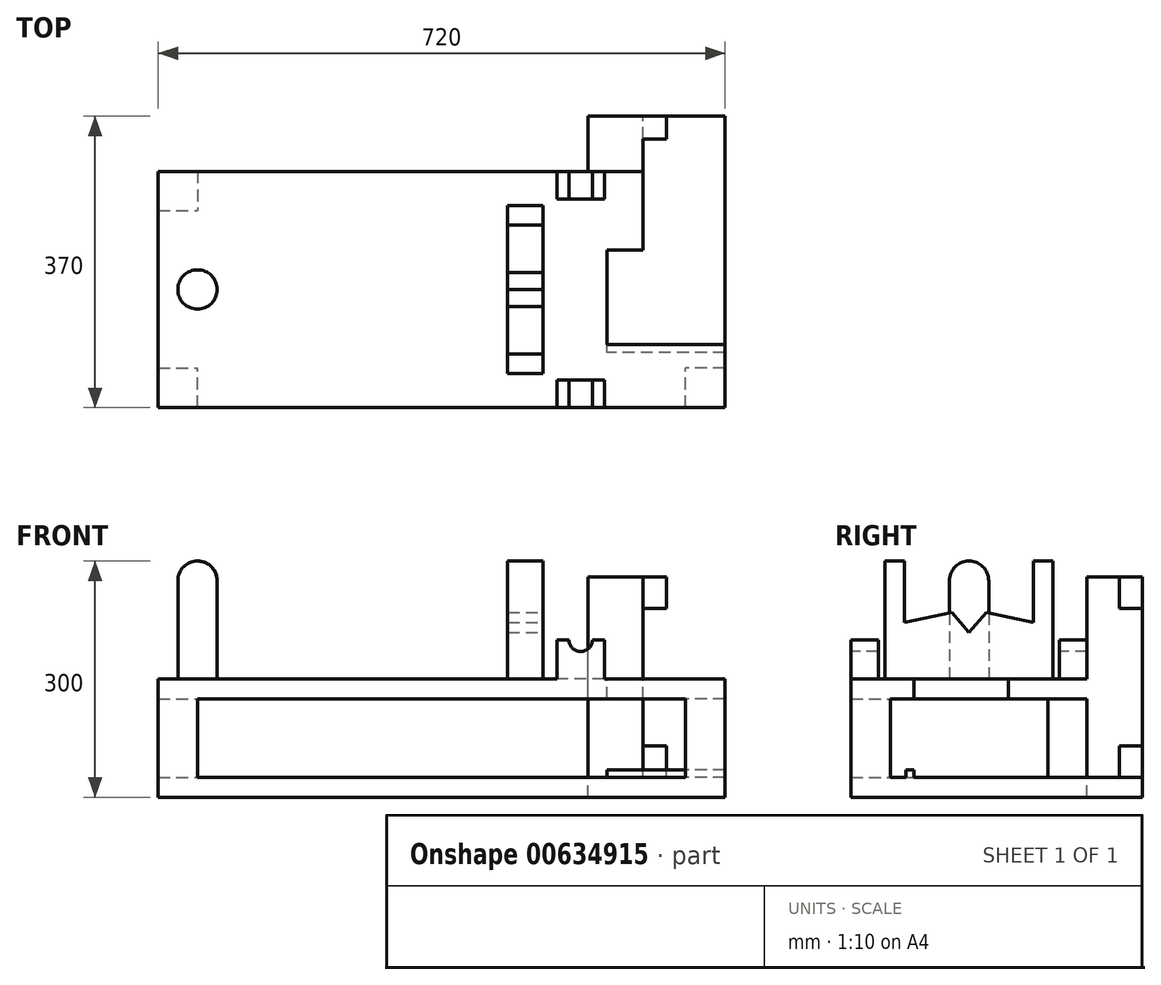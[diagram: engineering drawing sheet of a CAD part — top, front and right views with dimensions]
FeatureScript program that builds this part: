
annotation { "Feature Type Name" : "Feature", "Feature Type Description" : "" }
export const myFeature = defineFeature(function(context is Context, id is Id, definition is map)
    precondition{}
    {
        {
            var Q0;
            Q0=qCreatedBy(makeId("Top.planeOp"),FACE);
            var sketch = newSketch(context, id + "F0", { "sketchPlane" : qUnion([Q0])});
            skLineSegment(sketch, "E0.bottom", {"start": v(-360, 150) * mm, "end": v(360, 150) * mm});
            skLineSegment(sketch, "E0.top", {"start": v(-360, -150) * mm, "end": v(360, -150) * mm});
            skLineSegment(sketch, "E0.left", {"start": v(-360, 150) * mm, "end": v(-360, -150) * mm});
            skLineSegment(sketch, "E0.right", {"start": v(360, 150) * mm, "end": v(360, -150) * mm});
            skSolve(sketch);
        }
        {
            var Q0;
            Q0=makeQuery(id+"F0.imprint","IMPRINT",FACE,{"disambiguationData":[TD([[makeQuery(id+"F0.imprint","IMPRINT",EDGE,{"derivedFrom":sQuery(id+"F0.wireOp",EDGE,"E0.bottom")}),-1.0]])]});
            extrude(context, id + "F1", {"entities" : qUnion([Q0]), "depth" : 25 * mm, "offsetDistance" : 25 * mm});
        }
        {
            var Q0;
            Q0=makeQuery(id+"F1.opExtrude","CAP_FACE",FACE,{"disambiguationData":[OSD([sQuery(id+"F0.wireOp",EDGE,"E0.bottom"),sQuery(id+"F0.wireOp",EDGE,"E0.top"),sQuery(id+"F0.wireOp",EDGE,"E0.left"),sQuery(id+"F0.wireOp",EDGE,"E0.right")])],"isStart":false});
            var sketch = newSketch(context, id + "F2", { "sketchPlane" : qUnion([Q0])});
            skLineSegment(sketch, "E1.bottom", {"start": v(-360, -150) * mm, "end": v(-310, -150) * mm});
            skLineSegment(sketch, "E1.top", {"start": v(-360, -100) * mm, "end": v(-310, -100) * mm});
            skLineSegment(sketch, "E1.left", {"start": v(-360, -150) * mm, "end": v(-360, -100) * mm});
            skLineSegment(sketch, "E1.right", {"start": v(-310, -150) * mm, "end": v(-310, -100) * mm});
            skSolve(sketch);
        }
        {
            var Q0;
            Q0=makeQuery(id+"F2.imprint","IMPRINT",FACE,{"disambiguationData":[TD([[makeQuery(id+"F2.imprint","IMPRINT",EDGE,{"derivedFrom":sQuery(id+"F2.wireOp",EDGE,"E1.bottom")}),1.0]])]});
            extrude(context, id + "F3", {"entities" : qUnion([Q0]), "operationType" : NewBodyOperationType.ADD, "depth" : 100 * mm, "offsetDistance" : 25 * mm});
        }
        {
            var Q0;
            Q0=makeQuery(id+"F1.opExtrude","CAP_FACE",FACE,{"disambiguationData":[OSD([sQuery(id+"F0.wireOp",EDGE,"E0.bottom"),sQuery(id+"F0.wireOp",EDGE,"E0.top"),sQuery(id+"F0.wireOp",EDGE,"E0.left"),sQuery(id+"F0.wireOp",EDGE,"E0.right")])],"isStart":false});
            var sketch = newSketch(context, id + "F4", { "sketchPlane" : qUnion([Q0])});
            skLineSegment(sketch, "E2.bottom", {"start": v(360, -150) * mm, "end": v(310, -150) * mm});
            skLineSegment(sketch, "E2.top", {"start": v(360, -100) * mm, "end": v(310, -100) * mm});
            skLineSegment(sketch, "E2.left", {"start": v(360, -150) * mm, "end": v(360, -100) * mm});
            skLineSegment(sketch, "E2.right", {"start": v(310, -150) * mm, "end": v(310, -100) * mm});
            skLineSegment(sketch, "E3.bottom", {"start": v(360, 150) * mm, "end": v(310, 150) * mm});
            skLineSegment(sketch, "E3.top", {"start": v(360, 100) * mm, "end": v(310, 100) * mm});
            skLineSegment(sketch, "E3.left", {"start": v(360, 150) * mm, "end": v(360, 100) * mm});
            skLineSegment(sketch, "E3.right", {"start": v(310, 150) * mm, "end": v(310, 100) * mm});
            skLineSegment(sketch, "E4.bottom", {"start": v(-360, 150) * mm, "end": v(-310, 150) * mm});
            skLineSegment(sketch, "E4.top", {"start": v(-360, 100) * mm, "end": v(-310, 100) * mm});
            skLineSegment(sketch, "E4.left", {"start": v(-360, 150) * mm, "end": v(-360, 100) * mm});
            skLineSegment(sketch, "E4.right", {"start": v(-310, 150) * mm, "end": v(-310, 100) * mm});
            skSolve(sketch);
        }
        {
            var Q0;
            Q0=makeQuery(id+"F4.imprint","IMPRINT",FACE,{"disambiguationData":[TD([[makeQuery(id+"F4.imprint","IMPRINT",EDGE,{"derivedFrom":sQuery(id+"F4.wireOp",EDGE,"E2.bottom")}),1.0]])]});
            var Q1;
            Q1=makeQuery(id+"F4.imprint","IMPRINT",FACE,{"disambiguationData":[TD([[makeQuery(id+"F4.imprint","IMPRINT",EDGE,{"derivedFrom":sQuery(id+"F4.wireOp",EDGE,"E4.bottom")}),-1.0]])]});
            var Q2;
            Q2=makeQuery(id+"F4.imprint","IMPRINT",FACE,{"disambiguationData":[TD([[makeQuery(id+"F4.imprint","IMPRINT",EDGE,{"derivedFrom":sQuery(id+"F4.wireOp",EDGE,"E3.bottom")}),-1.0]])]});
            extrude(context, id + "F5", {"entities" : qUnion([Q0, Q1, Q2]), "operationType" : NewBodyOperationType.ADD, "depth" : 100 * mm, "offsetDistance" : 25 * mm});
        }
        {
            var Q0;
            Q0=makeQuery(id+"F5.opExtrude","CAP_FACE",FACE,{"disambiguationData":[OSD([sQuery(id+"F4.wireOp",EDGE,"E4.bottom"),sQuery(id+"F4.wireOp",EDGE,"E4.top"),sQuery(id+"F4.wireOp",EDGE,"E4.left"),sQuery(id+"F4.wireOp",EDGE,"E4.right")])],"isStart":false});
            var sketch = newSketch(context, id + "F6", { "sketchPlane" : qUnion([Q0])});
            skLineSegment(sketch, "E5.bottom", {"start": v(-360, 150) * mm, "end": v(360, 150) * mm});
            skLineSegment(sketch, "E5.top", {"start": v(-360, -150) * mm, "end": v(360, -150) * mm});
            skLineSegment(sketch, "E5.left", {"start": v(-360, 150) * mm, "end": v(-360, -150) * mm});
            skLineSegment(sketch, "E5.right", {"start": v(360, 150) * mm, "end": v(360, -150) * mm});
            skSolve(sketch);
        }
        {
            var Q0;
            {var subQ4=makeQuery(id+"F5.opExtrude","CAP_EDGE",EDGE,{"disambiguationData":[OSD([sQuery(id+"F4.wireOp",EDGE,"E4.top")])],"isStart":false});Q0=makeQuery(id+"F6.imprint","IMPRINT",FACE,{"disambiguationData":[TD([[makeQuery(id+"F6.imprint","IMPRINT",EDGE,{"derivedFrom":subQ4}),1.0]])]});}
            var Q1;
            {var subQ3=sQuery(id+"F6.wireOp",EDGE,"E5.top");Q1=makeQuery(id+"F6.imprint","IMPRINT",FACE,{"disambiguationData":[TD([[makeQuery(id+"F6.imprint","IMPRINT",EDGE,{"derivedFrom":subQ3}),1.0]])]});}
            extrude(context, id + "F7", {"entities" : qUnion([Q0, Q1]), "operationType" : NewBodyOperationType.ADD, "depth" : 25 * mm, "offsetDistance" : 25 * mm});
        }
        {
            var Q0;
            Q0=makeQuery(id+"F7.opExtrude","CAP_FACE",FACE,{"disambiguationData":[OSD([sQuery(id+"F6.wireOp",EDGE,"E5.bottom"),sQuery(id+"F6.wireOp",EDGE,"E5.top"),sQuery(id+"F6.wireOp",EDGE,"E5.left"),sQuery(id+"F6.wireOp",EDGE,"E5.right")])],"isStart":false});
            var sketch = newSketch(context, id + "F8", { "sketchPlane" : qUnion([Q0])});
            skCircle(sketch, "E6", {"center": v(-310, 0) * mm, "radius": 25 * mm});
            skSolve(sketch);
        }
        {
            var Q0;
            Q0=makeQuery(id+"F8.imprint","IMPRINT",FACE,{"disambiguationData":[TD([[makeQuery(id+"F8.imprint","IMPRINT",EDGE,{"derivedFrom":sQuery(id+"F8.wireOp",EDGE,"E6")}),1.0]])]});
            extrude(context, id + "F9", {"entities" : qUnion([Q0]), "operationType" : NewBodyOperationType.ADD, "depth" : 150 * mm, "offsetDistance" : 25 * mm});
        }
        {
            var Q0;
            Q0=makeQuery(id+"F7.opExtrude","CAP_FACE",FACE,{"disambiguationData":[OSD([sQuery(id+"F6.wireOp",EDGE,"E5.bottom"),sQuery(id+"F6.wireOp",EDGE,"E5.top"),sQuery(id+"F6.wireOp",EDGE,"E5.left"),sQuery(id+"F6.wireOp",EDGE,"E5.right")])],"isStart":false});
            var sketch = newSketch(context, id + "F10", { "sketchPlane" : qUnion([Q0])});
            skLineSegment(sketch, "E7.bottom", {"start": v(84, 106.83) * mm, "end": v(129, 106.83) * mm});
            skLineSegment(sketch, "E7.top", {"start": v(84, -106.83) * mm, "end": v(129, -106.83) * mm});
            skLineSegment(sketch, "E7.left", {"start": v(84, 106.83) * mm, "end": v(84, -106.83) * mm});
            skLineSegment(sketch, "E7.right", {"start": v(129, 106.83) * mm, "end": v(129, -106.83) * mm});
            skLineSegment(sketch, "E8", {"start": v(-360, 0) * mm, "end": v(360, 0) * mm});
            skSolve(sketch);
        }
        {
            var Q0;
            {var subQ0=sQuery(id+"F10.wireOp",EDGE,"E7.top");Q0=makeQuery(id+"F10.imprint","IMPRINT",FACE,{"disambiguationData":[TD([[makeQuery(id+"F10.imprint","IMPRINT",EDGE,{"derivedFrom":subQ0}),1.0]])]});}
            var Q1;
            {var subQ0=sQuery(id+"F10.wireOp",EDGE,"E7.bottom");Q1=makeQuery(id+"F10.imprint","IMPRINT",FACE,{"disambiguationData":[TD([[makeQuery(id+"F10.imprint","IMPRINT",EDGE,{"derivedFrom":subQ0}),-1.0]])]});}
            extrude(context, id + "F11", {"entities" : qUnion([Q0, Q1]), "operationType" : NewBodyOperationType.ADD, "depth" : 150 * mm, "offsetDistance" : 25 * mm});
        }
        {
            var Q0;
            Q0=makeQuery(id+"F11.opExtrude","SWEPT_FACE",FACE,{"disambiguationData":[OSD([sQuery(id+"F10.wireOp",EDGE,"E7.right")])]});
            var sketch = newSketch(context, id + "F12", { "sketchPlane" : qUnion([Q0])});
            skLineSegment(sketch, "E9", {"start": v(-81.83, 300) * mm, "end": v(-81.83, 221.94) * mm});
            skLineSegment(sketch, "E10", {"start": v(-81.83, 221.94) * mm, "end": v(-21.83, 234.49) * mm});
            skLineSegment(sketch, "E11", {"start": v(-21.83, 234.49) * mm, "end": v(0, 209.4) * mm});
            skLineSegment(sketch, "E12", {"start": v(0, 209.4) * mm, "end": v(21.83, 234.49) * mm});
            skLineSegment(sketch, "E13", {"start": v(21.83, 234.49) * mm, "end": v(81.83, 221.94) * mm});
            skLineSegment(sketch, "E14", {"start": v(81.83, 221.94) * mm, "end": v(81.83, 300) * mm});
            skLineSegment(sketch, "E15", {"start": v(-81.83, 300) * mm, "end": v(81.83, 300) * mm});
            skSolve(sketch);
        }
        {
            var Q0;
            Q0 = qSketchRegion(id + "F12", true);
            extrude(context, id + "F13", {"entities" : qUnion([Q0]), "operationType" : NewBodyOperationType.REMOVE, "oppositeDirection" : true, "depth" : 50 * mm, "offsetDistance" : 25 * mm});
        }
        {
            var Q0;
            Q0=makeQuery(id+"F7.opExtrude","CAP_FACE",FACE,{"disambiguationData":[OSD([sQuery(id+"F6.wireOp",EDGE,"E5.bottom"),sQuery(id+"F6.wireOp",EDGE,"E5.top"),sQuery(id+"F6.wireOp",EDGE,"E5.left"),sQuery(id+"F6.wireOp",EDGE,"E5.right")])],"isStart":false});
            var sketch = newSketch(context, id + "F14", { "sketchPlane" : qUnion([Q0])});
            skLineSegment(sketch, "E16.bottom", {"start": v(186, 150) * mm, "end": v(256, 150) * mm});
            skLineSegment(sketch, "E16.top", {"start": v(186, 220) * mm, "end": v(256, 220) * mm});
            skLineSegment(sketch, "E16.left", {"start": v(186, 150) * mm, "end": v(186, 220) * mm});
            skLineSegment(sketch, "E16.right", {"start": v(256, 150) * mm, "end": v(256, 220) * mm});
            skSolve(sketch);
        }
        {
            var Q0;
            Q0 = qSketchRegion(id + "F14", true);
            extrude(context, id + "F15", {"entities" : qUnion([Q0]), "operationType" : NewBodyOperationType.ADD, "oppositeDirection" : true, "depth" : 150 * mm, "offsetDistance" : 25 * mm});
        }
        {
            var Q0;
            Q0 = qSketchRegion(id + "F14", true);
            extrude(context, id + "F16", {"entities" : qUnion([Q0]), "operationType" : NewBodyOperationType.ADD, "depth" : 130 * mm, "offsetDistance" : 25 * mm});
        }
        {
            var Q0;
            Q0=makeQuery(id+"F9.opExtrude","CAP_FACE",FACE,{"disambiguationData":[OSD([sQuery(id+"F8.wireOp",EDGE,"E6")])],"isStart":false});
            fillet(context, id + "F17", {"entities" : qUnion([Q0]), "radius" : 25 * mm, "tangentPropagation" : true, "allowEdgeOverflow" : false});
        }
        {
            var Q0;
            Q0=makeQuery(id+"F15.boolean.opBoolean","MERGE",FACE,{"derivedFrom":[makeQuery(id+"F7.opExtrude","CAP_FACE",FACE,{"disambiguationData":[OSD([sQuery(id+"F6.wireOp",EDGE,"E5.bottom"),sQuery(id+"F6.wireOp",EDGE,"E5.top"),sQuery(id+"F6.wireOp",EDGE,"E5.left"),sQuery(id+"F6.wireOp",EDGE,"E5.right")])],"isStart":false}),makeQuery(id+"F15.opExtrude","CAP_FACE",FACE,{"disambiguationData":[OSD([sQuery(id+"F14.wireOp",EDGE,"E16.bottom"),sQuery(id+"F14.wireOp",EDGE,"E16.top"),sQuery(id+"F14.wireOp",EDGE,"E16.left"),sQuery(id+"F14.wireOp",EDGE,"E16.right")])],"isStart":true})]});
            var sketch = newSketch(context, id + "F18", { "sketchPlane" : qUnion([Q0])});
            skLineSegment(sketch, "E17.bottom", {"start": v(360, -70) * mm, "end": v(210, -70) * mm});
            skLineSegment(sketch, "E17.top", {"start": v(360, 50) * mm, "end": v(210, 50) * mm});
            skLineSegment(sketch, "E17.left", {"start": v(360, -70) * mm, "end": v(360, 50) * mm});
            skLineSegment(sketch, "E17.right", {"start": v(210, -70) * mm, "end": v(210, 50) * mm});
            skSolve(sketch);
        }
        {
            var Q0;
            Q0 = qSketchRegion(id + "F18", true);
            extrude(context, id + "F19", {"entities" : qUnion([Q0]), "operationType" : NewBodyOperationType.REMOVE, "oppositeDirection" : true, "depth" : 25 * mm, "offsetDistance" : 25 * mm});
        }
        {
            var Q0;
            Q0=makeQuery(id+"F15.boolean.opBoolean","MERGE",FACE,{"derivedFrom":[makeQuery(id+"F7.opExtrude","CAP_FACE",FACE,{"disambiguationData":[OSD([sQuery(id+"F6.wireOp",EDGE,"E5.bottom"),sQuery(id+"F6.wireOp",EDGE,"E5.top"),sQuery(id+"F6.wireOp",EDGE,"E5.left"),sQuery(id+"F6.wireOp",EDGE,"E5.right")])],"isStart":false}),makeQuery(id+"F15.opExtrude","CAP_FACE",FACE,{"disambiguationData":[OSD([sQuery(id+"F14.wireOp",EDGE,"E16.bottom"),sQuery(id+"F14.wireOp",EDGE,"E16.top"),sQuery(id+"F14.wireOp",EDGE,"E16.left"),sQuery(id+"F14.wireOp",EDGE,"E16.right")])],"isStart":true})]});
            var sketch = newSketch(context, id + "F20", { "sketchPlane" : qUnion([Q0])});
            skLineSegment(sketch, "E18.bottom", {"start": v(146.66, -150) * mm, "end": v(206.66, -150) * mm});
            skLineSegment(sketch, "E18.top", {"start": v(146.66, -115) * mm, "end": v(206.66, -115) * mm});
            skLineSegment(sketch, "E18.left", {"start": v(146.66, -150) * mm, "end": v(146.66, -115) * mm});
            skLineSegment(sketch, "E18.right", {"start": v(206.66, -150) * mm, "end": v(206.66, -115) * mm});
            skLineSegment(sketch, "E19.bottom", {"start": v(206.66, 150) * mm, "end": v(146.66, 150) * mm});
            skLineSegment(sketch, "E19.top", {"start": v(206.66, 115) * mm, "end": v(146.66, 115) * mm});
            skLineSegment(sketch, "E19.left", {"start": v(206.66, 150) * mm, "end": v(206.66, 115) * mm});
            skLineSegment(sketch, "E19.right", {"start": v(146.66, 150) * mm, "end": v(146.66, 115) * mm});
            skSolve(sketch);
        }
        {
            var Q0;
            Q0 = qSketchRegion(id + "F20", true);
            extrude(context, id + "F21", {"entities" : qUnion([Q0]), "operationType" : NewBodyOperationType.ADD, "depth" : 50 * mm, "offsetDistance" : 25 * mm});
        }
        {
            var Q0;
            Q0=makeQuery(id+"F21.boolean.opBoolean","MERGE",FACE,{"derivedFrom":[makeQuery(id+"F7.boolean.opBoolean","MERGE",FACE,{"derivedFrom":[makeQuery(id+"F5.boolean.opBoolean","MERGE",FACE,{"derivedFrom":[makeQuery(id+"F3.boolean.opBoolean","MERGE",FACE,{"derivedFrom":[makeQuery(id+"F1.opExtrude","SWEPT_FACE",FACE,{"disambiguationData":[OSD([sQuery(id+"F0.wireOp",EDGE,"E0.top")])]}),makeQuery(id+"F3.opExtrude","SWEPT_FACE",FACE,{"disambiguationData":[OSD([sQuery(id+"F2.wireOp",EDGE,"E1.bottom")])]})]}),makeQuery(id+"F5.opExtrude","SWEPT_FACE",FACE,{"disambiguationData":[OSD([sQuery(id+"F4.wireOp",EDGE,"E2.bottom")])]})]}),makeQuery(id+"F7.opExtrude","SWEPT_FACE",FACE,{"disambiguationData":[OSD([sQuery(id+"F6.wireOp",EDGE,"E5.top")])]})]}),makeQuery(id+"F21.opExtrude","SWEPT_FACE",FACE,{"disambiguationData":[OSD([sQuery(id+"F20.wireOp",EDGE,"E18.bottom")])]})]});
            var sketch = newSketch(context, id + "F22", { "sketchPlane" : qUnion([Q0])});
            skArc(sketch, "E20", {"start": v(161.66, 200) * mm, "mid": v(176.66, 185) * mm, "end": v(191.66, 200) * mm});
            skSolve(sketch);
        }
        {
            var Q0;
            {var subQ0=sQuery(id+"F22.wireOp",EDGE,"E20");Q0=makeQuery(id+"F22.imprint","IMPRINT",FACE,{"disambiguationData":[TD([[makeQuery(id+"F22.imprint","IMPRINT",EDGE,{"derivedFrom":subQ0}),1.0]])]});}
            extrude(context, id + "F23", {"entities" : qUnion([Q0]), "operationType" : NewBodyOperationType.REMOVE, "oppositeDirection" : true, "depth" : 300 * mm, "hasOffset" : true, "offsetDistance" : 300 * mm});
        }
        {
            var Q0;
            Q0=makeQuery(id+"F15.boolean.opBoolean","MERGE",FACE,{"derivedFrom":[makeQuery(id+"F7.opExtrude","CAP_FACE",FACE,{"disambiguationData":[OSD([sQuery(id+"F6.wireOp",EDGE,"E5.bottom"),sQuery(id+"F6.wireOp",EDGE,"E5.top"),sQuery(id+"F6.wireOp",EDGE,"E5.left"),sQuery(id+"F6.wireOp",EDGE,"E5.right")])],"isStart":false}),makeQuery(id+"F15.opExtrude","CAP_FACE",FACE,{"disambiguationData":[OSD([sQuery(id+"F14.wireOp",EDGE,"E16.bottom"),sQuery(id+"F14.wireOp",EDGE,"E16.top"),sQuery(id+"F14.wireOp",EDGE,"E16.left"),sQuery(id+"F14.wireOp",EDGE,"E16.right")])],"isStart":true})]});
            var sketch = newSketch(context, id + "F24", { "sketchPlane" : qUnion([Q0])});
            skLineSegment(sketch, "E21.bottom", {"start": v(360, 150) * mm, "end": v(256, 150) * mm});
            skLineSegment(sketch, "E21.top", {"start": v(360, 50) * mm, "end": v(256, 50) * mm});
            skLineSegment(sketch, "E21.left", {"start": v(360, 150) * mm, "end": v(360, 50) * mm});
            skLineSegment(sketch, "E21.right", {"start": v(256, 150) * mm, "end": v(256, 50) * mm});
            skSolve(sketch);
        }
        {
            var Q0;
            Q0 = qSketchRegion(id + "F24", true);
            extrude(context, id + "F25", {"entities" : qUnion([Q0]), "operationType" : NewBodyOperationType.REMOVE, "oppositeDirection" : true, "depth" : 150 * mm, "offsetDistance" : 25 * mm});
        }
        {
            var Q0;
            Q0=makeQuery(id+"F1.opExtrude","CAP_FACE",FACE,{"disambiguationData":[OSD([sQuery(id+"F0.wireOp",EDGE,"E0.bottom"),sQuery(id+"F0.wireOp",EDGE,"E0.top"),sQuery(id+"F0.wireOp",EDGE,"E0.left"),sQuery(id+"F0.wireOp",EDGE,"E0.right")])],"isStart":false});
            var sketch = newSketch(context, id + "F26", { "sketchPlane" : qUnion([Q0])});
            skLineSegment(sketch, "E22.bottom", {"start": v(360, 50) * mm, "end": v(256, 50) * mm});
            skLineSegment(sketch, "E22.top", {"start": v(360, 220) * mm, "end": v(256, 220) * mm});
            skLineSegment(sketch, "E22.left", {"start": v(360, 50) * mm, "end": v(360, 220) * mm});
            skLineSegment(sketch, "E22.right", {"start": v(256, 50) * mm, "end": v(256, 220) * mm});
            skSolve(sketch);
        }
        {
            var Q0;
            Q0 = qSketchRegion(id + "F26", true);
            extrude(context, id + "F27", {"entities" : qUnion([Q0]), "operationType" : NewBodyOperationType.ADD, "oppositeDirection" : true, "depth" : 25 * mm, "offsetDistance" : 25 * mm});
        }
        {
            var Q0;
            {var subQ0=sQuery(id+"F14.wireOp",EDGE,"E16.right");Q0=makeQuery(id+"F25.boolean.opBoolean","MERGE",FACE,{"derivedFrom":[makeQuery(id+"F16.boolean.opBoolean","MERGE",FACE,{"derivedFrom":[makeQuery(id+"F15.opExtrude","SWEPT_FACE",FACE,{"disambiguationData":[OSD([subQ0])]}),makeQuery(id+"F16.opExtrude","SWEPT_FACE",FACE,{"disambiguationData":[OSD([subQ0])]})]}),makeQuery(id+"F25.opExtrude","SWEPT_FACE",FACE,{"disambiguationData":[OSD([sQuery(id+"F24.wireOp",EDGE,"E21.right")])]})]});}
            var sketch = newSketch(context, id + "F28", { "sketchPlane" : qUnion([Q0])});
            skLineSegment(sketch, "E23.bottom", {"start": v(191, 280) * mm, "end": v(220, 280) * mm});
            skLineSegment(sketch, "E23.top", {"start": v(191, 240) * mm, "end": v(220, 240) * mm});
            skLineSegment(sketch, "E23.left", {"start": v(191, 280) * mm, "end": v(191, 240) * mm});
            skLineSegment(sketch, "E23.right", {"start": v(220, 280) * mm, "end": v(220, 240) * mm});
            skLineSegment(sketch, "E24.bottom", {"start": v(191, 25) * mm, "end": v(220, 25) * mm});
            skLineSegment(sketch, "E24.top", {"start": v(191, 65) * mm, "end": v(220, 65) * mm});
            skLineSegment(sketch, "E24.left", {"start": v(191, 25) * mm, "end": v(191, 65) * mm});
            skLineSegment(sketch, "E24.right", {"start": v(220, 25) * mm, "end": v(220, 65) * mm});
            skSolve(sketch);
        }
        {
            var Q0;
            Q0 = qSketchRegion(id + "F28", true);
            extrude(context, id + "F29", {"entities" : qUnion([Q0]), "operationType" : NewBodyOperationType.ADD, "depth" : 30 * mm, "offsetDistance" : 25 * mm});
        }
        {
            var Q0;
            Q0=makeQuery(id+"F27.boolean.opBoolean","MERGE",FACE,{"derivedFrom":[makeQuery(id+"F1.opExtrude","CAP_FACE",FACE,{"disambiguationData":[OSD([sQuery(id+"F0.wireOp",EDGE,"E0.bottom"),sQuery(id+"F0.wireOp",EDGE,"E0.top"),sQuery(id+"F0.wireOp",EDGE,"E0.left"),sQuery(id+"F0.wireOp",EDGE,"E0.right")])],"isStart":false}),makeQuery(id+"F27.opExtrude","CAP_FACE",FACE,{"disambiguationData":[OSD([sQuery(id+"F26.wireOp",EDGE,"E22.bottom"),sQuery(id+"F26.wireOp",EDGE,"E22.top"),sQuery(id+"F26.wireOp",EDGE,"E22.left"),sQuery(id+"F26.wireOp",EDGE,"E22.right")])],"isStart":true})]});
            var sketch = newSketch(context, id + "F30", { "sketchPlane" : qUnion([Q0])});
            skLineSegment(sketch, "E25.bottom", {"start": v(360, -80) * mm, "end": v(210, -80) * mm});
            skLineSegment(sketch, "E25.top", {"start": v(360, -70) * mm, "end": v(210, -70) * mm});
            skLineSegment(sketch, "E25.left", {"start": v(360, -80) * mm, "end": v(360, -70) * mm});
            skLineSegment(sketch, "E25.right", {"start": v(210, -80) * mm, "end": v(210, -70) * mm});
            skSolve(sketch);
        }
        {
            var Q0;
            Q0 = qSketchRegion(id + "F30", true);
            extrude(context, id + "F31", {"entities" : qUnion([Q0]), "operationType" : NewBodyOperationType.ADD, "depth" : 10 * mm, "offsetDistance" : 25 * mm});
        }
    });
